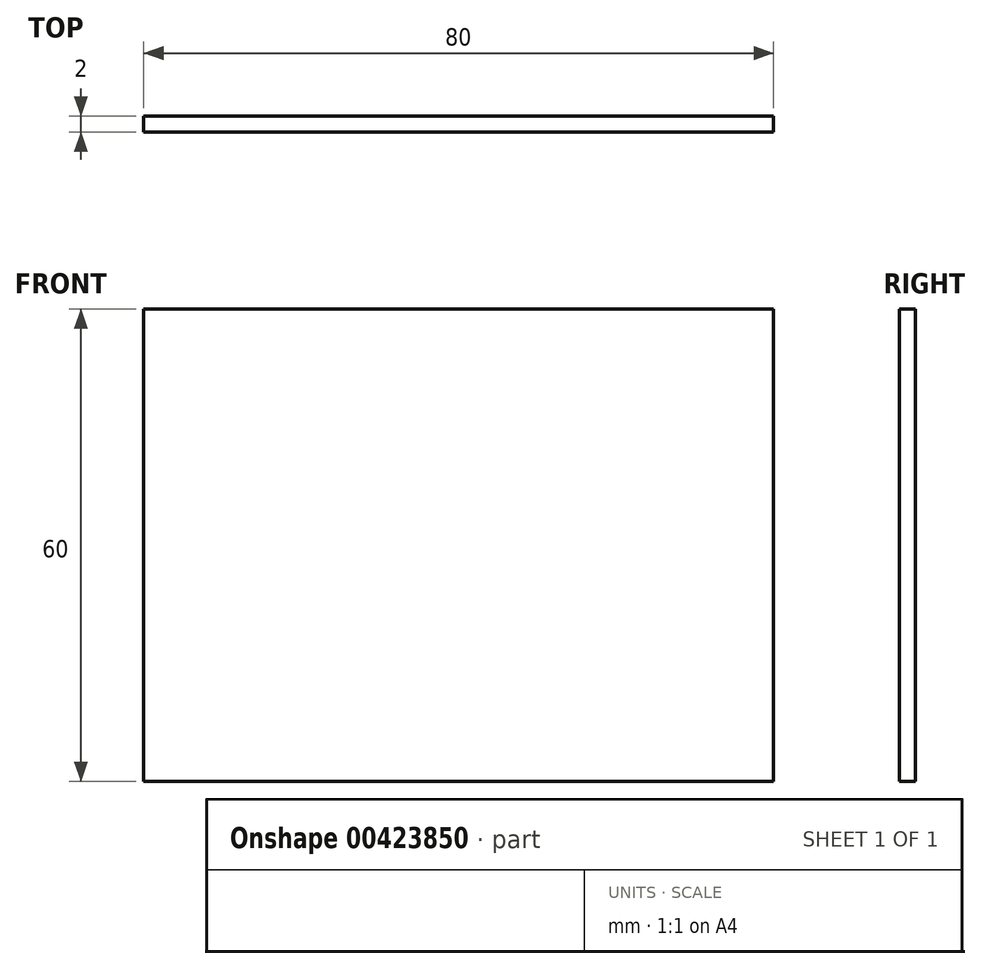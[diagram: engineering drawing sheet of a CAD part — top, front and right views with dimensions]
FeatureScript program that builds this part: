
annotation { "Feature Type Name" : "Feature", "Feature Type Description" : "" }
export const myFeature = defineFeature(function(context is Context, id is Id, definition is map)
    precondition{}
    {
        {
            var Q0;
            Q0=qCreatedBy(makeId("Front.planeOp"),FACE);
            var sketch = newSketch(context, id + "F0", { "sketchPlane" : qUnion([Q0])});
            skLineSegment(sketch, "E0.bottom", {"start": v(40, -30) * mm, "end": v(-40, -30) * mm});
            skLineSegment(sketch, "E0.top", {"start": v(40, 30) * mm, "end": v(-40, 30) * mm});
            skLineSegment(sketch, "E0.left", {"start": v(40, -30) * mm, "end": v(40, 30) * mm});
            skLineSegment(sketch, "E0.right", {"start": v(-40, -30) * mm, "end": v(-40, 30) * mm});
            skPoint(sketch, "E0.middle", {"position": v(0, 0) * mm});
            skSolve(sketch);
        }
        {
            var Q0;
            Q0=qSketchRegion(id+"F0",true);
            extrude(context, id + "F1", {"entities" : qUnion([Q0]), "depth" : 2 * mm});
        }
    });
